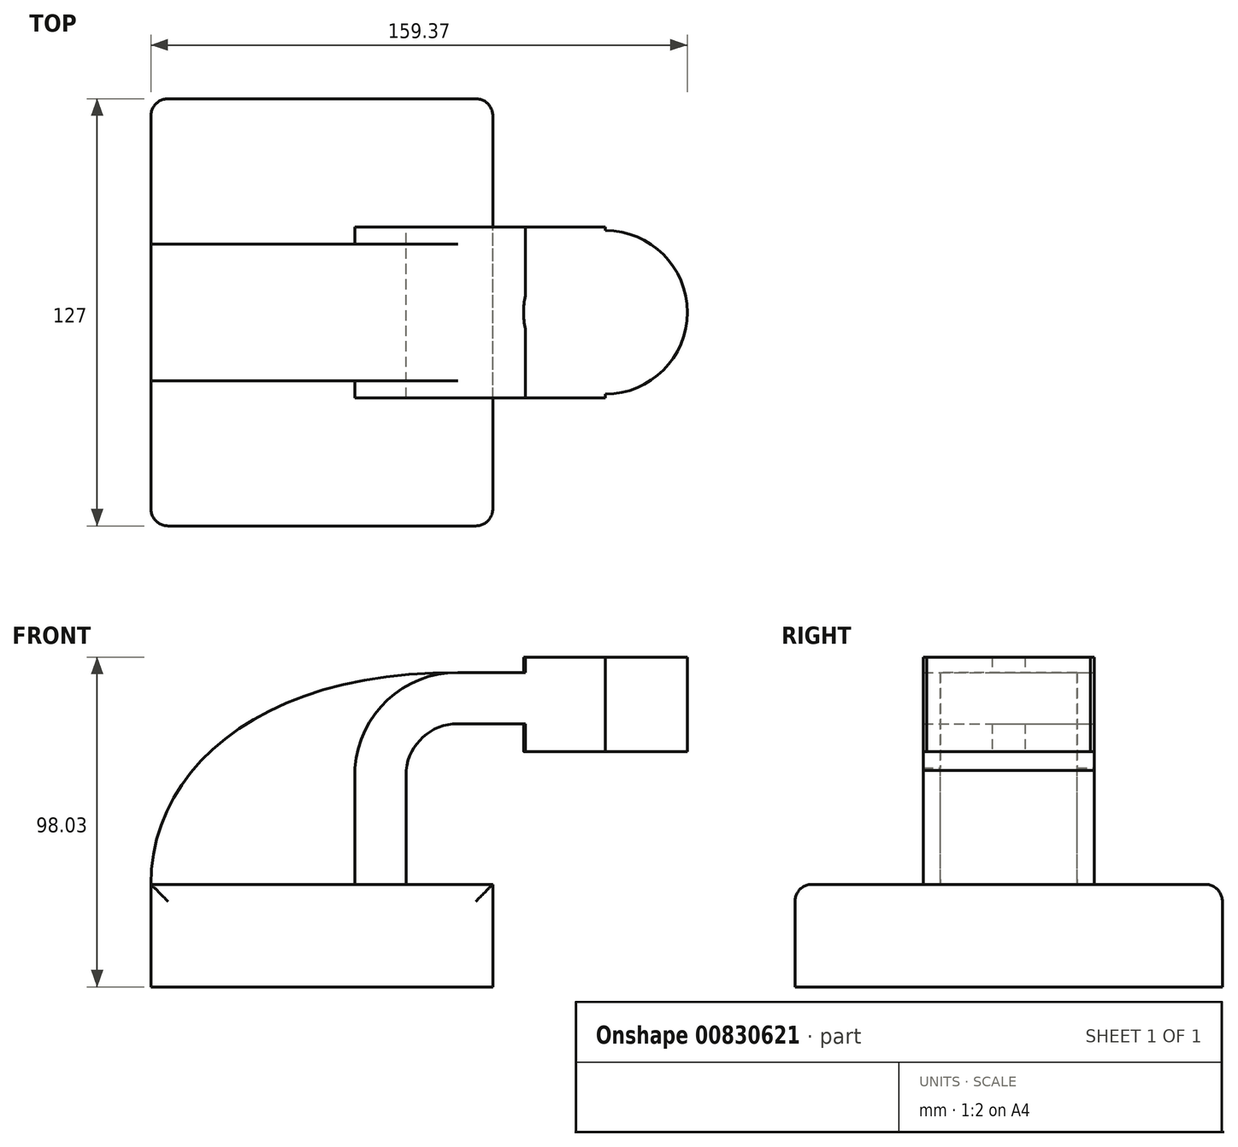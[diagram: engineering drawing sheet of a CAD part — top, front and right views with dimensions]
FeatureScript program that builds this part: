
annotation { "Feature Type Name" : "Feature", "Feature Type Description" : "" }
export const myFeature = defineFeature(function(context is Context, id is Id, definition is map)
    precondition{}
    {
        {
            var Q0;
            Q0=qCreatedBy(makeId("Front.planeOp"),FACE);
            var sketch = newSketch(context, id + "F0", { "sketchPlane" : qUnion([Q0])});
            skLineSegment(sketch, "E0.bottom", {"start": v(-50.8, 15.24) * mm, "end": v(50.8, 15.24) * mm});
            skLineSegment(sketch, "E0.top", {"start": v(-50.8, -15.24) * mm, "end": v(50.8, -15.24) * mm});
            skLineSegment(sketch, "E0.left", {"start": v(-50.8, 15.24) * mm, "end": v(-50.8, -15.24) * mm});
            skLineSegment(sketch, "E0.right", {"start": v(50.8, 15.24) * mm, "end": v(50.8, -15.24) * mm});
            skPoint(sketch, "E0.middle", {"position": v(0, 0) * mm});
            skLineSegment(sketch, "E1.bottom", {"start": v(108.57, 54.7) * mm, "end": v(60.41, 54.7) * mm});
            skLineSegment(sketch, "E1.top", {"start": v(108.57, 82.79) * mm, "end": v(60.41, 82.79) * mm});
            skLineSegment(sketch, "E1.left", {"start": v(108.57, 54.7) * mm, "end": v(108.57, 82.79) * mm});
            skLineSegment(sketch, "E1.right", {"start": v(60.41, 54.7) * mm, "end": v(60.41, 82.79) * mm});
            skPoint(sketch, "E1.middle", {"position": v(84.5, 68.74) * mm});
            skLineSegment(sketch, "E2", {"start": v(25.05, 15.24) * mm, "end": v(25.05, 49.16) * mm});
            skLineSegment(sketch, "E3", {"start": v(84.24, 63) * mm, "end": v(40.35, 63) * mm});
            skArc(sketch, "E4", {"start": v(40.35, 63) * mm, "mid": v(30.04, 59.02) * mm, "end": v(25.05, 49.16) * mm});
            skLineSegment(sketch, "E5.0", {"start": v(9.8, 16.66) * mm, "end": v(9.8, 49.8) * mm});
            skArc(sketch, "E5.1", {"start": v(40.35, 78.23) * mm, "mid": v(19.49, 70.02) * mm, "end": v(9.8, 49.8) * mm});
            skLineSegment(sketch, "E5.2", {"start": v(84.24, 78.23) * mm, "end": v(40.35, 78.23) * mm});
            skLineSegment(sketch, "E6", {"start": v(84.24, 54.7) * mm, "end": v(84.24, 82.79) * mm});
            skPoint(sketch, "E6.endSnap0", {"position": v(84.5, 82.79) * mm});
            skFitSpline(sketch, "E7", {"points": [v(-50.8, 15.24) * mm, v(40.35, 78.23) * mm], "startDerivative": vector(0.33, 105.58) * mm, "endDerivative": vector(172.3, -0.87) * mm});
            skLineSegment(sketch, "E8", {"start": v(9.8, 16.66) * mm, "end": v(9.82, 10.82) * mm});
            skSolve(sketch);
        }
        {
            var Q0;
            Q0=makeQuery(id+"F0.imprint","IMPRINT",FACE,{"disambiguationData":[TD([[makeQuery(id+"F0.imprint","IMPRINT",EDGE,{"derivedFrom":sQuery(id+"F0.wireOp",EDGE,"E0.top")}),1.0]])]});
            var Q1;
            Q1=sQuery(id+"F0.wireOp",EDGE,"E0.bottom");
            var Q2;
            Q2=sQuery(id+"F0.wireOp",EDGE,"E0.right");
            var Q3;
            Q3=sQuery(id+"F0.wireOp",EDGE,"E0.top");
            var Q4;
            Q4=sQuery(id+"F0.wireOp",EDGE,"E0.left");
            extrude(context, id + "F1", {"entities" : qUnion([Q0]), "surfaceEntities" : qUnion([Q1, Q2, Q3, Q4]), "endBound" : BoundingType.SYMMETRIC, "depth" : 127 * mm, "offsetDistance" : 25.4 * mm});
        }
        {
            var Q0;
            Q0=makeQuery(id+"F1.opExtrude","CAP_EDGE",EDGE,{"disambiguationData":[OSD([sQuery(id+"F0.wireOp",EDGE,"E0.bottom")])],"isStart":false});
            var Q1;
            Q1=makeQuery(id+"F1.opExtrude","CAP_EDGE",EDGE,{"disambiguationData":[OSD([sQuery(id+"F0.wireOp",EDGE,"E0.right")])],"isStart":false});
            var Q2;
            Q2=makeQuery(id+"F1.opExtrude","CAP_EDGE",EDGE,{"disambiguationData":[OSD([sQuery(id+"F0.wireOp",EDGE,"E0.right")])],"isStart":true});
            var Q3;
            Q3=makeQuery(id+"F1.opExtrude","CAP_EDGE",EDGE,{"disambiguationData":[OSD([sQuery(id+"F0.wireOp",EDGE,"E0.left")])],"isStart":false});
            var Q4;
            Q4=makeQuery(id+"F1.opExtrude","CAP_EDGE",EDGE,{"disambiguationData":[OSD([sQuery(id+"F0.wireOp",EDGE,"E0.left")])],"isStart":true});
            var Q5;
            Q5=makeQuery(id+"F1.opExtrude","CAP_EDGE",EDGE,{"disambiguationData":[OSD([sQuery(id+"F0.wireOp",EDGE,"E0.bottom")])],"isStart":true});
            fillet(context, id + "F2", {"entities" : qUnion([Q0, Q1, Q2, Q3, Q4, Q5]), "radius" : 5.08 * mm, "tangentPropagation" : true, "allowEdgeOverflow" : false});
        }
        {
            var Q0;
            {var subQ0=sQuery(id+"F0.wireOp",EDGE,"E2");Q0=makeQuery(id+"F0.imprint","IMPRINT",FACE,{"disambiguationData":[TD([[makeQuery(id+"F0.imprint","IMPRINT",EDGE,{"derivedFrom":subQ0}),1.0]])]});}
            var Q1;
            {var subQ0=sQuery(id+"F0.wireOp",EDGE,"E3");var subQ1=sQuery(id+"F0.wireOp",EDGE,"E1.right");var subQ2=makeQuery(id+"F0.imprint","INTERSECT",VERTEX,{"derivedFrom":[subQ1,subQ0]});Q1=makeQuery(id+"F0.imprint","IMPRINT",FACE,{"disambiguationData":[TD([[makeQuery(id+"F0.imprint","IMPRINT",EDGE,{"disambiguationData":[TD([[subQ2,-1.0]])],"derivedFrom":subQ1}),-1.0]])]});}
            var Q2;
            {var subQ0=sQuery(id+"F0.wireOp",EDGE,"E1.right");var subQ1=sQuery(id+"F0.wireOp",EDGE,"E1.top");var subQ2=makeQuery(id+"F0.imprint","INTERSECT",VERTEX,{"derivedFrom":[subQ1,subQ0]});Q2=makeQuery(id+"F0.imprint","IMPRINT",FACE,{"disambiguationData":[TD([[makeQuery(id+"F0.imprint","IMPRINT",EDGE,{"disambiguationData":[TD([[subQ2,1.0]])],"derivedFrom":subQ1}),1.0]])]});}
            var Q3;
            {var subQ0=sQuery(id+"F0.wireOp",EDGE,"E1.right");var subQ1=sQuery(id+"F0.wireOp",EDGE,"E1.bottom");var subQ2=makeQuery(id+"F0.imprint","INTERSECT",VERTEX,{"derivedFrom":[subQ1,subQ0]});Q3=makeQuery(id+"F0.imprint","IMPRINT",FACE,{"disambiguationData":[TD([[makeQuery(id+"F0.imprint","IMPRINT",EDGE,{"disambiguationData":[TD([[subQ2,1.0]])],"derivedFrom":subQ1}),-1.0]])]});}
            extrude(context, id + "F3", {"entities" : qUnion([Q0, Q1, Q2, Q3]), "operationType" : NewBodyOperationType.ADD, "endBound" : BoundingType.SYMMETRIC, "depth" : 50.8 * mm, "offsetDistance" : 25.4 * mm});
        }
        {
            var Q0;
            {var subQ0=sQuery(id+"F0.wireOp",EDGE,"E5.0");Q0=makeQuery(id+"F0.imprint","IMPRINT",FACE,{"disambiguationData":[TD([[makeQuery(id+"F0.imprint","IMPRINT",EDGE,{"derivedFrom":subQ0}),1.0]])]});}
            extrude(context, id + "F4", {"entities" : qUnion([Q0]), "operationType" : NewBodyOperationType.ADD, "endBound" : BoundingType.SYMMETRIC, "depth" : 40.64 * mm, "offsetDistance" : 25.4 * mm});
        }
        {
            var Q0;
            {var subQ4=sQuery(id+"F0.wireOp",EDGE,"E1.left");Q0=makeQuery(id+"F0.imprint","IMPRINT",FACE,{"disambiguationData":[TD([[makeQuery(id+"F0.imprint","IMPRINT",EDGE,{"derivedFrom":subQ4}),1.0]])]});}
            var Q1;
            Q1=sQuery(id+"F0.wireOp",EDGE,"E6");
            revolve(context, id + "F5", {"operationType" : NewBodyOperationType.ADD, "surfaceOperationType" : NewSurfaceOperationType.NEW, "entities" : qUnion([Q0]), "axis" : qUnion([Q1]), "revolveType" : RevolveType.SYMMETRIC, "angle" : 360 * degree});
        }
    });
